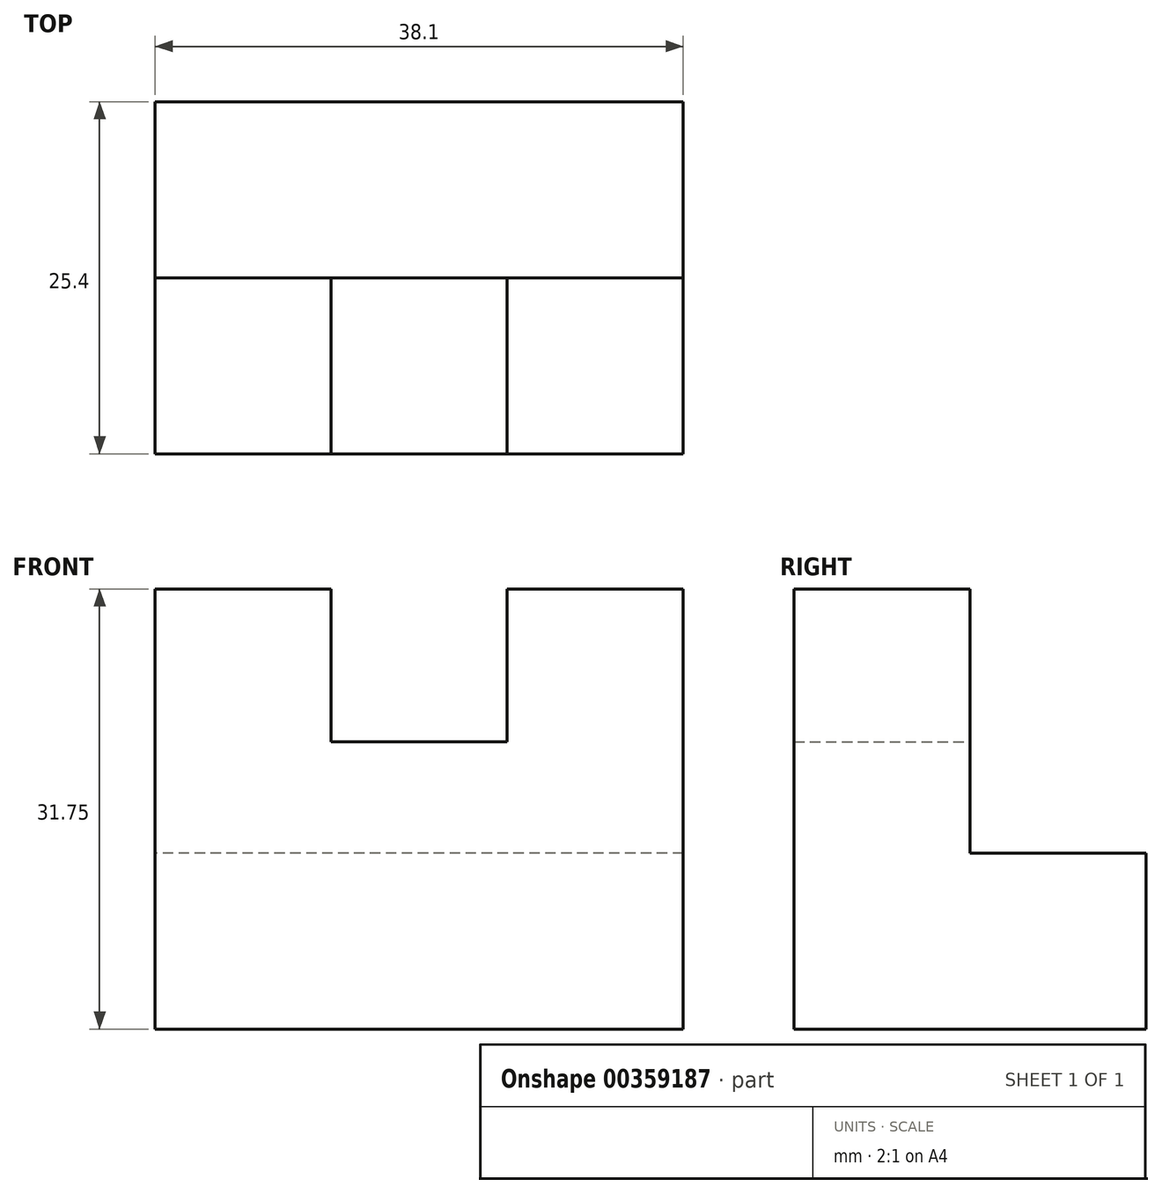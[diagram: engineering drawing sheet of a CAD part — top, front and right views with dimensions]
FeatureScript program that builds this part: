
annotation { "Feature Type Name" : "Feature", "Feature Type Description" : "" }
export const myFeature = defineFeature(function(context is Context, id is Id, definition is map)
    precondition{}
    {
        {
            var Q0;
            Q0=qCreatedBy(makeId("Front.planeOp"),FACE);
            var sketch = newSketch(context, id + "F0", { "sketchPlane" : qUnion([Q0])});
            skLineSegment(sketch, "E0", {"start": v(0, 0) * mm, "end": v(38.1, 0) * mm});
            skLineSegment(sketch, "E1", {"start": v(38.1, 0) * mm, "end": v(38.1, 31.75) * mm});
            skLineSegment(sketch, "E2", {"start": v(38.1, 31.75) * mm, "end": v(25.4, 31.75) * mm});
            skLineSegment(sketch, "E3", {"start": v(25.4, 31.75) * mm, "end": v(25.4, 20.71) * mm});
            skLineSegment(sketch, "E4", {"start": v(25.4, 20.71) * mm, "end": v(12.7, 20.71) * mm});
            skLineSegment(sketch, "E5", {"start": v(12.7, 20.71) * mm, "end": v(12.7, 31.75) * mm});
            skLineSegment(sketch, "E6", {"start": v(12.7, 31.75) * mm, "end": v(0, 31.75) * mm});
            skLineSegment(sketch, "E7", {"start": v(0, 31.75) * mm, "end": v(0, 0) * mm});
            skSolve(sketch);
        }
        {
            var Q0;
            Q0 = qSketchRegion(id + "F0", true);
            extrude(context, id + "F1", {"entities" : qUnion([Q0]), "depth" : 25.4 * mm});
        }
        {
            var Q0;
            Q0=makeQuery(id+"F1.opExtrude","CAP_FACE",FACE,{"disambiguationData":[OSD([sQuery(id+"F0.wireOp",EDGE,"E0"),sQuery(id+"F0.wireOp",EDGE,"E1"),sQuery(id+"F0.wireOp",EDGE,"E2"),sQuery(id+"F0.wireOp",EDGE,"E3"),sQuery(id+"F0.wireOp",EDGE,"E4"),sQuery(id+"F0.wireOp",EDGE,"E5"),sQuery(id+"F0.wireOp",EDGE,"E6"),sQuery(id+"F0.wireOp",EDGE,"E7")])],"isStart":true});
            var sketch = newSketch(context, id + "F2", { "sketchPlane" : qUnion([Q0])});
            skLineSegment(sketch, "E8", {"start": v(-38.1, 12.7) * mm, "end": v(0, 12.7) * mm});
            skSolve(sketch);
        }
        {
            var Q0;
            {var subQ1=sQuery(id+"F2.wireOp",EDGE,"E8");Q0=makeQuery(id+"F2.imprint","IMPRINT",FACE,{"disambiguationData":[TD([[makeQuery(id+"F2.imprint","IMPRINT",EDGE,{"derivedFrom":subQ1}),1.0]])]});}
            extrude(context, id + "F3", {"entities" : qUnion([Q0]), "operationType" : NewBodyOperationType.REMOVE, "oppositeDirection" : true, "depth" : 12.7 * mm});
        }
    });
